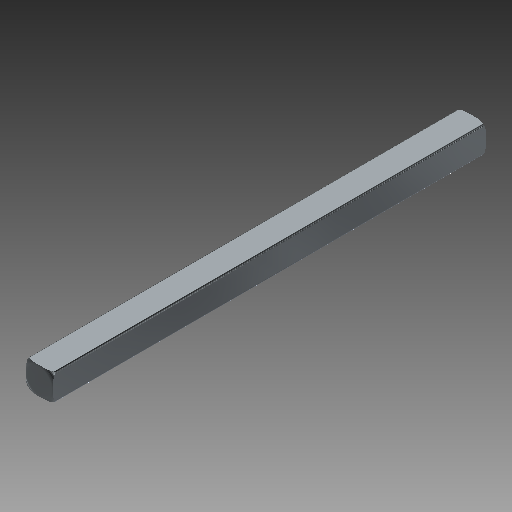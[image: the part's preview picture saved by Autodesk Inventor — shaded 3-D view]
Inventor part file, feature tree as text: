
AUTODESK INVENTOR PART (.ipt)
format: ipt  version: 2018 (Build 220112000, 112)  size: 181,248 bytes
history: native  units: in
note: dims shown in document units (in); Inventor stores cm internally (conversion verified against a paired STEP export)
features: sketch x2, plane x2, extrude x1, revolve x1, mirror x1, other x1
ambient origin geometry x8: Origin, YZ Plane, XZ Plane, XY Plane, X Axis, Y Axis, Z Axis, Center Point
bodies: Solid1 (feature_tree)
feature tree (8):
  sketch  "Sketch1"  dims[d0=2.0in d1=0.0in d2=90.0deg]
  extrude  "Extrusion1"  TaperAngle=90.0deg  [1 undecoded]
  plane  "Work Plane1"
  revolve  "Revolution1"  [1 undecoded]
  plane  "Work Plane2"
  mirror  "Mirror1"
  other  "Work Axis1"
  sketch  "Sketch2"  dims[d3=90.0deg]
note: 2 required parameter values undecoded (feature->parameter linkage not recoverable at this tier; creation-order binding heuristic only, values carry confidence <= 0.55)
